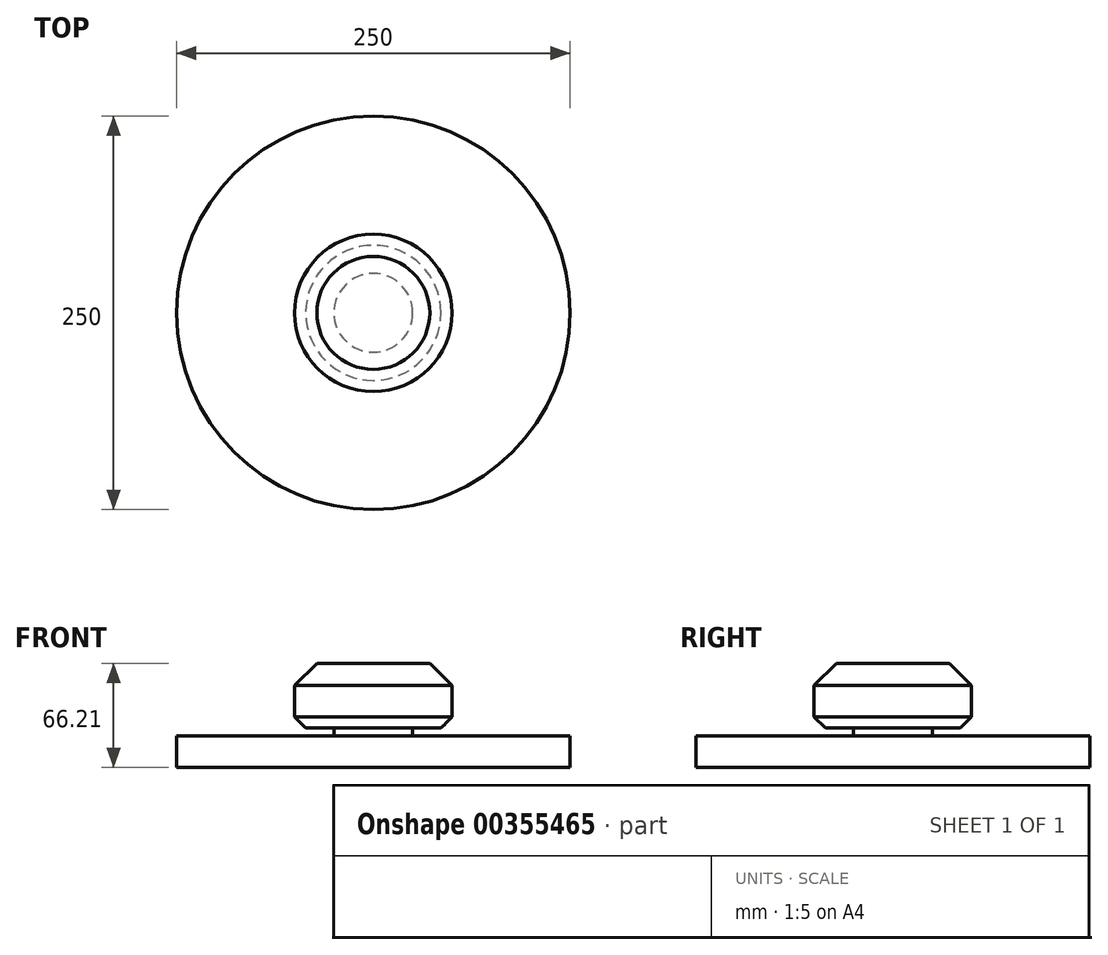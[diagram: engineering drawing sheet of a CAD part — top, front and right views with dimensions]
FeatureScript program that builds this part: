
annotation { "Feature Type Name" : "Feature", "Feature Type Description" : "" }
export const myFeature = defineFeature(function(context is Context, id is Id, definition is map)
    precondition{}
    {
        {
            var Q0;
            Q0=qCreatedBy(makeId("Top.planeOp"),FACE);
            var sketch = newSketch(context, id + "F0", { "sketchPlane" : qUnion([Q0])});
            skCircle(sketch, "E0", {"center": v(0, 0) * mm, "radius": 50 * mm});
            skSolve(sketch);
        }
        {
            var Q0;
            Q0=makeQuery(id+"F0.imprint","IMPRINT",FACE,{"disambiguationData":[TD([[makeQuery(id+"F0.imprint","IMPRINT",EDGE,{"derivedFrom":sQuery(id+"F0.wireOp",EDGE,"E0")}),1.0]])]});
            extrude(context, id + "F1", {"entities" : qUnion([Q0]), "depth" : 24.14 * mm, "hasSecondDirection" : true, "secondDirectionOppositeDirection" : true, "secondDirectionDepth" : 17.07 * mm});
        }
        {
            var Q0;
            Q0=makeQuery(id+"F1.opExtrude","CAP_EDGE",EDGE,{"disambiguationData":[OSD([sQuery(id+"F0.wireOp",EDGE,"E0")])],"isStart":false});
            chamfer(context, id + "F2", {"entities" : qUnion([Q0]), "width" : 14.14 * mm, "tangentPropagation" : true});
        }
        {
            var Q0;
            Q0=makeQuery(id+"F1.opExtrude","CAP_EDGE",EDGE,{"disambiguationData":[OSD([sQuery(id+"F0.wireOp",EDGE,"E0")])],"isStart":true});
            chamfer(context, id + "F3", {"entities" : qUnion([Q0]), "width" : 7.07 * mm, "tangentPropagation" : true});
        }
        {
            var Q0;
            Q0=makeQuery(id+"F1.opExtrude","CAP_FACE",FACE,{"disambiguationData":[OSD([sQuery(id+"F0.wireOp",EDGE,"E0")])],"isStart":true});
            var sketch = newSketch(context, id + "F4", { "sketchPlane" : qUnion([Q0])});
            skCircle(sketch, "E1", {"center": v(0, 0) * mm, "radius": 25 * mm});
            skSolve(sketch);
        }
        {
            var Q0;
            Q0=makeQuery(id+"F4.imprint","IMPRINT",FACE,{"disambiguationData":[TD([[makeQuery(id+"F4.imprint","IMPRINT",EDGE,{"derivedFrom":sQuery(id+"F4.wireOp",EDGE,"E1")}),1.0]])]});
            extrude(context, id + "F5", {"entities" : qUnion([Q0]), "depth" : 5 * mm});
        }
        {
            var Q0;
            Q0=makeQuery(id+"F5.opExtrude","CAP_FACE",FACE,{"disambiguationData":[OSD([sQuery(id+"F4.wireOp",EDGE,"E1")])],"isStart":false});
            var sketch = newSketch(context, id + "F6", { "sketchPlane" : qUnion([Q0])});
            skCircle(sketch, "E2", {"center": v(0, 0) * mm, "radius": 125 * mm});
            skSolve(sketch);
        }
        {
            var Q0;
            Q0=makeQuery(id+"F6.imprint","IMPRINT",FACE,{"disambiguationData":[TD([[makeQuery(id+"F6.imprint","IMPRINT",EDGE,{"derivedFrom":makeQuery(id+"F5.opExtrude","CAP_EDGE",EDGE,{"disambiguationData":[OSD([sQuery(id+"F4.wireOp",EDGE,"E1")])],"isStart":false})}),1.0]])]});
            var Q1;
            Q1=makeQuery(id+"F6.imprint","IMPRINT",FACE,{"disambiguationData":[TD([[makeQuery(id+"F6.imprint","IMPRINT",EDGE,{"derivedFrom":sQuery(id+"F6.wireOp",EDGE,"E2")}),1.0]])]});
            extrude(context, id + "F7", {"entities" : qUnion([Q0, Q1]), "depth" : 20 * mm});
        }
        {
            var Q0;
            Q0=makeQuery(id+"F1.opExtrude","CAP_FACE",FACE,{"disambiguationData":[OSD([sQuery(id+"F0.wireOp",EDGE,"E0")])],"isStart":false});
            var sketch = newSketch(context, id + "F8", { "sketchPlane" : qUnion([Q0])});
            skLineSegment(sketch, "E3", {"start": v(0, 35.86) * mm, "end": v(0, 30.86) * mm, "construction": true});
            skCircle(sketch, "E4.cCircle", {"center": v(0, 0) * mm, "radius": 30.86 * mm, "construction": true});
            skLineSegment(sketch, "E4.0", {"start": v(0, 30.86) * mm, "end": v(26.72, 15.43) * mm, "construction": true});
            skLineSegment(sketch, "E4.1", {"start": v(26.72, 15.43) * mm, "end": v(26.72, -15.43) * mm, "construction": true});
            skLineSegment(sketch, "E4.2", {"start": v(26.72, -15.43) * mm, "end": v(0, -30.86) * mm, "construction": true});
            skLineSegment(sketch, "E4.3", {"start": v(0, -30.86) * mm, "end": v(-26.72, -15.43) * mm, "construction": true});
            skLineSegment(sketch, "E4.4", {"start": v(-26.72, -15.43) * mm, "end": v(-26.72, 15.43) * mm, "construction": true});
            skLineSegment(sketch, "E4.5", {"start": v(-26.72, 15.43) * mm, "end": v(0, 30.86) * mm, "construction": true});
            skLineSegment(sketch, "E5", {"start": v(26.72, 15.43) * mm, "end": v(31.05, 17.93) * mm, "construction": true});
            skLineSegment(sketch, "E6", {"start": v(26.72, -15.43) * mm, "end": v(31.05, -17.93) * mm, "construction": true});
            skLineSegment(sketch, "E7", {"start": v(0, -30.86) * mm, "end": v(0, -35.86) * mm, "construction": true});
            skLineSegment(sketch, "E8", {"start": v(-26.72, -15.43) * mm, "end": v(-31.05, -17.93) * mm, "construction": true});
            skLineSegment(sketch, "E9", {"start": v(-26.72, 15.43) * mm, "end": v(-31.05, 17.93) * mm, "construction": true});
            skSolve(sketch);
        }
        {
            var Q0;
            Q0=qCreatedBy(makeId("Top.planeOp"),FACE);
            cPlane(context, id + "F9", {"entities" : qUnion([Q0]), "cplaneType" : CPlaneType.OFFSET, "offset" : 5 * mm, "width" : 150 * mm, "height" : 150 * mm});
        }
        {
            var Q0;
            Q0=qCreatedBy(id+"F9.planeOp",FACE);
            var sketch = newSketch(context, id + "F10", { "sketchPlane" : qUnion([Q0])});
            skCircle(sketch, "E10", {"center": v(0, 0) * mm, "radius": 50 * mm, "construction": true});
            skLineSegment(sketch, "E11.0", {"start": v(0, 50) * mm, "end": v(43.3, 25) * mm, "construction": true});
            skLineSegment(sketch, "E11.1", {"start": v(43.3, 25) * mm, "end": v(43.3, -25) * mm, "construction": true});
            skLineSegment(sketch, "E11.2", {"start": v(43.3, -25) * mm, "end": v(0, -50) * mm, "construction": true});
            skLineSegment(sketch, "E11.3", {"start": v(0, -50) * mm, "end": v(-43.3, -25) * mm, "construction": true});
            skLineSegment(sketch, "E11.4", {"start": v(-43.3, -25) * mm, "end": v(-43.3, 25) * mm, "construction": true});
            skLineSegment(sketch, "E11.5", {"start": v(-43.3, 25) * mm, "end": v(0, 50) * mm, "construction": true});
            skSolve(sketch);
        }
        {
            var Q0;
            Q0=qCreatedBy(makeId("Top.planeOp"),FACE);
            cPlane(context, id + "F11", {"entities" : qUnion([Q0]), "cplaneType" : CPlaneType.OFFSET, "offset" : 5 * mm, "oppositeDirection" : true, "width" : 150 * mm, "height" : 150 * mm});
        }
        {
            var Q0;
            Q0=qCreatedBy(makeId("Top.planeOp"),FACE);
            cPlane(context, id + "F12", {"entities" : qUnion([Q0]), "cplaneType" : CPlaneType.OFFSET, "offset" : 13.54 * mm, "width" : 150 * mm, "height" : 150 * mm});
        }
        {
            var Q0;
            {var subQ0=sQuery(id+"F0.wireOp",EDGE,"E0");Q0=makeQuery(id+"F8.imprint","IMPRINT",FACE,{"disambiguationData":[TD([[makeQuery(id+"F8.imprint","IMPRINT",EDGE,{"derivedFrom":makeQuery(id+"F2.opChamfer","BLEND_EDGE",EDGE,{"blendedFrom":[makeQuery(id+"F1.opExtrude","CAP_EDGE",EDGE,{"disambiguationData":[OSD([subQ0])],"isStart":false}),makeQuery(id+"F1.opExtrude","CAP_FACE",FACE,{"disambiguationData":[OSD([subQ0])],"isStart":false})],"blendedInto":[makeQuery(id+"F1.opExtrude","CAP_FACE",FACE,{"disambiguationData":[OSD([subQ0])],"isStart":false})]})}),1.0]])]});}
            cPlane(context, id + "F13", {"entities" : qUnion([Q0]), "cplaneType" : CPlaneType.OFFSET, "offset" : 3.54 * mm, "oppositeDirection" : true, "width" : 150 * mm, "height" : 150 * mm});
        }
    });
